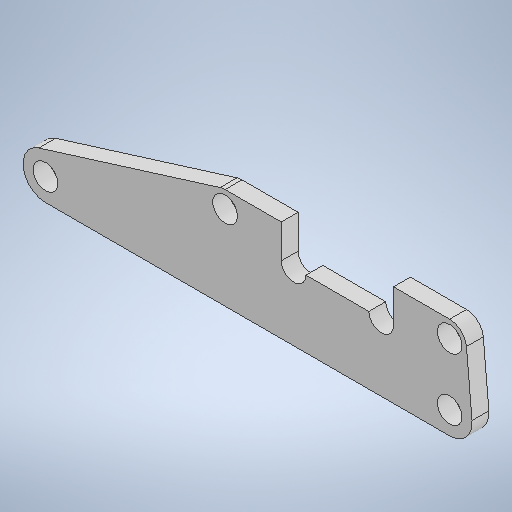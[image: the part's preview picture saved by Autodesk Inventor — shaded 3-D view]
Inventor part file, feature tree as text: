
AUTODESK INVENTOR PART (.ipt)
format: ipt  version: 2025.1 (Build 291241000, 241)  size: 266,240 bytes
history: native  units: mm
features: other x1, extrude x1, sketch x1
ambient origin geometry x8: Origin, YZ Plane, XZ Plane, XY Plane, X Axis, Y Axis, Z Axis, Center Point
bodies: Body1 (feature_tree)
feature tree (3):
  other  "ソリッド1"
  extrude  "押し出し1"  Depth=2.2mm
  sketch  "スケッチ1"
